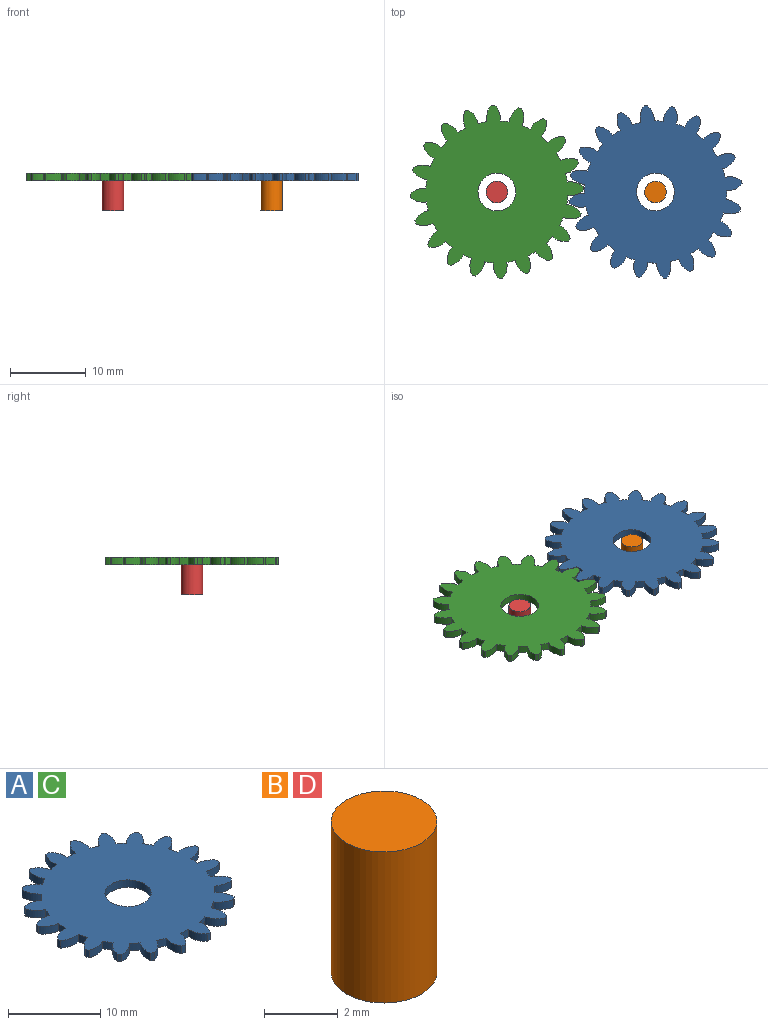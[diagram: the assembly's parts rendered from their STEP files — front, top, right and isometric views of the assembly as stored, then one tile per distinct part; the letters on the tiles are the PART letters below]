
ASSEMBLY  parts=4 mates=3
PART A: 83 faces, bbox 23x23x1 mm
  f0: cylinder r=2.61mm len=2.18mm, axis (0,0,-1), area 2.3mm2, adj f1,f79,f81,f82
  f1: cylinder r=9.41mm len=1.14mm, axis (0,0,-1), area 1.2mm2, adj f0,f2,f81,f82
  f2: cylinder r=2.61mm len=1.71mm, axis (0,0,-1), area 2.3mm2, adj f1,f3,f81,f82
  f3: plane 1x0.41mm, normal (-0.38,0.92,0), area 0.4mm2, adj f2,f4,f81,f82
  f4: cylinder r=2.61mm len=2.23mm, axis (0,0,-1), area 2.3mm2, adj f3,f5,f81,f82
  f5: cylinder r=9.41mm len=1mm, axis (0,0,-1), area 1.2mm2, adj f4,f6,f81,f82
  f6: cylinder r=2.61mm len=1.89mm, axis (0,0,-1), area 2.3mm2, adj f5,f7,f81,f82
  f7: plane 1x0.34mm, normal (-0.65,0.76,0), area 0.4mm2, adj f6,f8,f81,f82
  f8: cylinder r=2.61mm len=2.06mm, axis (0,0,-1), area 2.3mm2, adj f7,f9,f81,f82
  f9: cylinder r=9.41mm len=1mm, axis (0,0,-1), area 1.2mm2, adj f8,f10,f81,f82
  f10: cylinder r=2.61mm len=2.17mm, axis (0,0,-1), area 2.3mm2, adj f9,f11,f81,f82
  f11: plane 1x0.38mm, normal (-0.85,0.52,0), area 0.4mm2, adj f10,f12,f81,f82
  f12: cylinder r=2.61mm len=1.68mm, axis (0,0,-1), area 2.3mm2, adj f11,f13,f81,f82
  f13: cylinder r=9.41mm len=1.08mm, axis (0,0,-1), area 1.2mm2, adj f12,f14,f81,f82
  f14: cylinder r=2.61mm len=2.23mm, axis (0,0,-1), area 2.3mm2, adj f13,f15,f81,f82
  f15: plane 1x0.43mm, normal (-0.97,0.23,0), area 0.4mm2, adj f14,f16,f81,f82
  f16: cylinder r=2.61mm len=1.92mm, axis (0,0,-1), area 2.3mm2, adj f15,f17,f81,f82
  f17: cylinder r=9.41mm len=1.17mm, axis (0,0,-1), area 1.2mm2, adj f16,f18,f81,f82
  f18: cylinder r=2.61mm len=2.07mm, axis (0,0,-1), area 2.3mm2, adj f17,f19,f81,f82
  f19: plane 1x0.44mm, normal (-1,-0.08,0), area 0.4mm2, adj f18,f20,f81,f82
  f20: cylinder r=2.61mm len=2.18mm, axis (0,0,-1), area 2.3mm2, adj f19,f21,f81,f82
  f21: cylinder r=9.41mm len=1.14mm, axis (0,0,-1), area 1.2mm2, adj f20,f22,f81,f82
  f22: cylinder r=2.61mm len=1.71mm, axis (0,0,-1), area 2.3mm2, adj f21,f23,f81,f82
  f23: plane 1x0.41mm, normal (-0.92,-0.38,0), area 0.4mm2, adj f22,f24,f81,f82
  f24: cylinder r=2.61mm len=2.23mm, axis (0,0,-1), area 2.3mm2, adj f23,f25,f81,f82
  f25: cylinder r=9.41mm len=1mm, axis (0,0,-1), area 1.2mm2, adj f24,f26,f81,f82
  f26: cylinder r=2.61mm len=1.89mm, axis (0,0,-1), area 2.3mm2, adj f25,f27,f81,f82
  f27: plane 1x0.34mm, normal (-0.76,-0.65,0), area 0.4mm2, adj f26,f28,f81,f82
  f28: cylinder r=2.61mm len=2.06mm, axis (0,0,-1), area 2.3mm2, adj f27,f29,f81,f82
  f29: cylinder r=9.41mm len=1mm, axis (0,0,-1), area 1.2mm2, adj f28,f30,f81,f82
  f30: cylinder r=2.61mm len=2.17mm, axis (0,0,-1), area 2.3mm2, adj f29,f31,f81,f82
  f31: plane 1x0.38mm, normal (-0.52,-0.85,0), area 0.4mm2, adj f30,f32,f81,f82
  f32: cylinder r=2.61mm len=1.68mm, axis (0,0,-1), area 2.3mm2, adj f31,f33,f81,f82
  f33: cylinder r=9.41mm len=1.08mm, axis (0,0,-1), area 1.2mm2, adj f32,f34,f81,f82
  f34: cylinder r=2.61mm len=2.23mm, axis (0,0,-1), area 2.3mm2, adj f33,f35,f81,f82
  f35: plane 1x0.43mm, normal (-0.23,-0.97,0), area 0.4mm2, adj f34,f36,f81,f82
  f36: cylinder r=2.61mm len=1.92mm, axis (0,0,-1), area 2.3mm2, adj f35,f37,f81,f82
  f37: cylinder r=9.41mm len=1.17mm, axis (0,0,-1), area 1.2mm2, adj f36,f38,f81,f82
  f38: cylinder r=2.61mm len=2.07mm, axis (0,0,-1), area 2.3mm2, adj f37,f39,f81,f82
  f39: plane 1x0.44mm, normal (0.08,-1,0), area 0.4mm2, adj f38,f40,f81,f82
  f40: cylinder r=2.61mm len=2.18mm, axis (0,0,-1), area 2.3mm2, adj f39,f41,f81,f82
  f41: cylinder r=9.41mm len=1.14mm, axis (0,0,-1), area 1.2mm2, adj f40,f42,f81,f82
  f42: cylinder r=2.61mm len=1.71mm, axis (0,0,-1), area 2.3mm2, adj f41,f43,f81,f82
  f43: plane 1x0.41mm, normal (0.38,-0.92,0), area 0.4mm2, adj f42,f44,f81,f82
  f44: cylinder r=2.61mm len=2.23mm, axis (0,0,-1), area 2.3mm2, adj f43,f45,f81,f82
  f45: cylinder r=9.41mm len=1mm, axis (0,0,-1), area 1.2mm2, adj f44,f46,f81,f82
  f46: cylinder r=2.61mm len=1.89mm, axis (0,0,-1), area 2.3mm2, adj f45,f47,f81,f82
  f47: plane 1x0.34mm, normal (0.65,-0.76,0), area 0.4mm2, adj f46,f48,f81,f82
  f48: cylinder r=2.61mm len=2.06mm, axis (0,0,-1), area 2.3mm2, adj f47,f49,f81,f82
  f49: cylinder r=9.41mm len=1mm, axis (0,0,-1), area 1.2mm2, adj f48,f50,f81,f82
  f50: cylinder r=2.61mm len=2.17mm, axis (0,0,-1), area 2.3mm2, adj f49,f51,f81,f82
  f51: plane 1x0.38mm, normal (0.85,-0.52,0), area 0.4mm2, adj f50,f52,f81,f82
  f52: cylinder r=2.61mm len=1.68mm, axis (0,0,-1), area 2.3mm2, adj f51,f53,f81,f82
  f53: cylinder r=9.41mm len=1.08mm, axis (0,0,-1), area 1.2mm2, adj f52,f54,f81,f82
  f54: cylinder r=2.61mm len=2.23mm, axis (0,0,-1), area 2.3mm2, adj f53,f55,f81,f82
  f55: plane 1x0.43mm, normal (0.97,-0.23,0), area 0.4mm2, adj f54,f56,f81,f82
  f56: cylinder r=2.61mm len=1.92mm, axis (0,0,-1), area 2.3mm2, adj f55,f57,f81,f82
  f57: cylinder r=9.41mm len=1.17mm, axis (0,0,-1), area 1.2mm2, adj f56,f58,f81,f82
  f58: cylinder r=2.61mm len=2.07mm, axis (0,0,-1), area 2.3mm2, adj f57,f59,f81,f82
  f59: plane 1x0.44mm, normal (1,0.08,0), area 0.4mm2, adj f58,f60,f81,f82
  f60: cylinder r=2.61mm len=2.18mm, axis (0,0,-1), area 2.3mm2, adj f59,f61,f81,f82
  f61: cylinder r=9.41mm len=1.14mm, axis (0,0,-1), area 1.2mm2, adj f60,f62,f81,f82
  f62: cylinder r=2.61mm len=1.71mm, axis (0,0,-1), area 2.3mm2, adj f61,f63,f81,f82
  f63: plane 1x0.41mm, normal (0.92,0.38,0), area 0.4mm2, adj f62,f64,f81,f82
  f64: cylinder r=2.61mm len=2.23mm, axis (0,0,-1), area 2.3mm2, adj f63,f65,f81,f82
  f65: cylinder r=9.41mm len=1mm, axis (0,0,-1), area 1.2mm2, adj f64,f66,f81,f82
  f66: cylinder r=2.61mm len=1.89mm, axis (0,0,-1), area 2.3mm2, adj f65,f67,f81,f82
  f67: plane 1x0.34mm, normal (0.76,0.65,0), area 0.4mm2, adj f66,f68,f81,f82
  f68: cylinder r=2.61mm len=2.06mm, axis (0,0,-1), area 2.3mm2, adj f67,f69,f81,f82
  f69: cylinder r=9.41mm len=1mm, axis (0,0,-1), area 1.2mm2, adj f68,f70,f81,f82
  f70: cylinder r=2.61mm len=2.17mm, axis (0,0,-1), area 2.3mm2, adj f69,f71,f81,f82
  f71: plane 1x0.38mm, normal (0.52,0.85,0), area 0.4mm2, adj f70,f72,f81,f82
  f72: cylinder r=2.61mm len=1.68mm, axis (0,0,-1), area 2.3mm2, adj f71,f73,f81,f82
  f73: cylinder r=9.41mm len=1.08mm, axis (0,0,-1), area 1.2mm2, adj f72,f74,f81,f82
  f74: cylinder r=2.61mm len=2.23mm, axis (0,0,-1), area 2.3mm2, adj f73,f75,f81,f82
  f75: plane 1x0.43mm, normal (0.23,0.97,0), area 0.4mm2, adj f74,f76,f81,f82
  f76: cylinder r=2.61mm len=1.92mm, axis (0,0,-1), area 2.3mm2, adj f75,f77,f81,f82
  f77: cylinder r=9.41mm len=1.17mm, axis (0,0,-1), area 1.2mm2, adj f76,f78,f81,f82
  f78: cylinder r=2.61mm len=2.07mm, axis (0,0,-1), area 2.3mm2, adj f77,f79,f81,f82
  f79: plane 1x0.44mm, normal (-0.08,1,0), area 0.4mm2, adj f0,f78,f81,f82
  f80: cylinder r=2.5mm len=5mm, axis (0,0,-1), area 15.7mm2, adj f81,f82
  f81: plane 22.96x22.96mm, normal (0,0,1), area 320mm2, adj f0,f1,f2,f3,f4,f5,f6,f7
  f82: plane 22.96x22.96mm, normal (0,0,-1), area 320mm2, adj f0,f1,f2,f3,f4,f5,f6,f7
PART B: 3 faces, bbox 2.9x2.9x5 mm
  f0: cylinder r=1.43mm len=5mm, axis (0,0,-1), area 44.9mm2, adj f1,f2
  f1: plane 2.86x2.86mm, normal (0,0,1), area 6.4mm2, adj f0
  f2: plane 2.86x2.86mm, normal (0,0,-1), area 6.4mm2, adj f0
PART C: same geometry as A
PART D: same geometry as B
PLACE A rot(axis=(0,0,1),55.9deg) t=(7.76,1.3,4)mm
PLACE B t=(-8.22,-0.03,0)mm
PLACE C rot(axis=(0,0,-1),55.9deg) t=(-13.24,1.3,4)mm
PLACE D t=(-29.22,-0.03,0)mm fixed
MATE revolute C.f1 <-> D.f0  axis (0,0,1) through (-13.24,1.3,5)mm
MATE revolute A.f1 <-> B.f0  axis (0,0,1) through (7.76,1.3,5)mm
MATE fastened D.f0 <-> B.f1  axis (0,0,1) through (-13.24,1.3,5)mm
